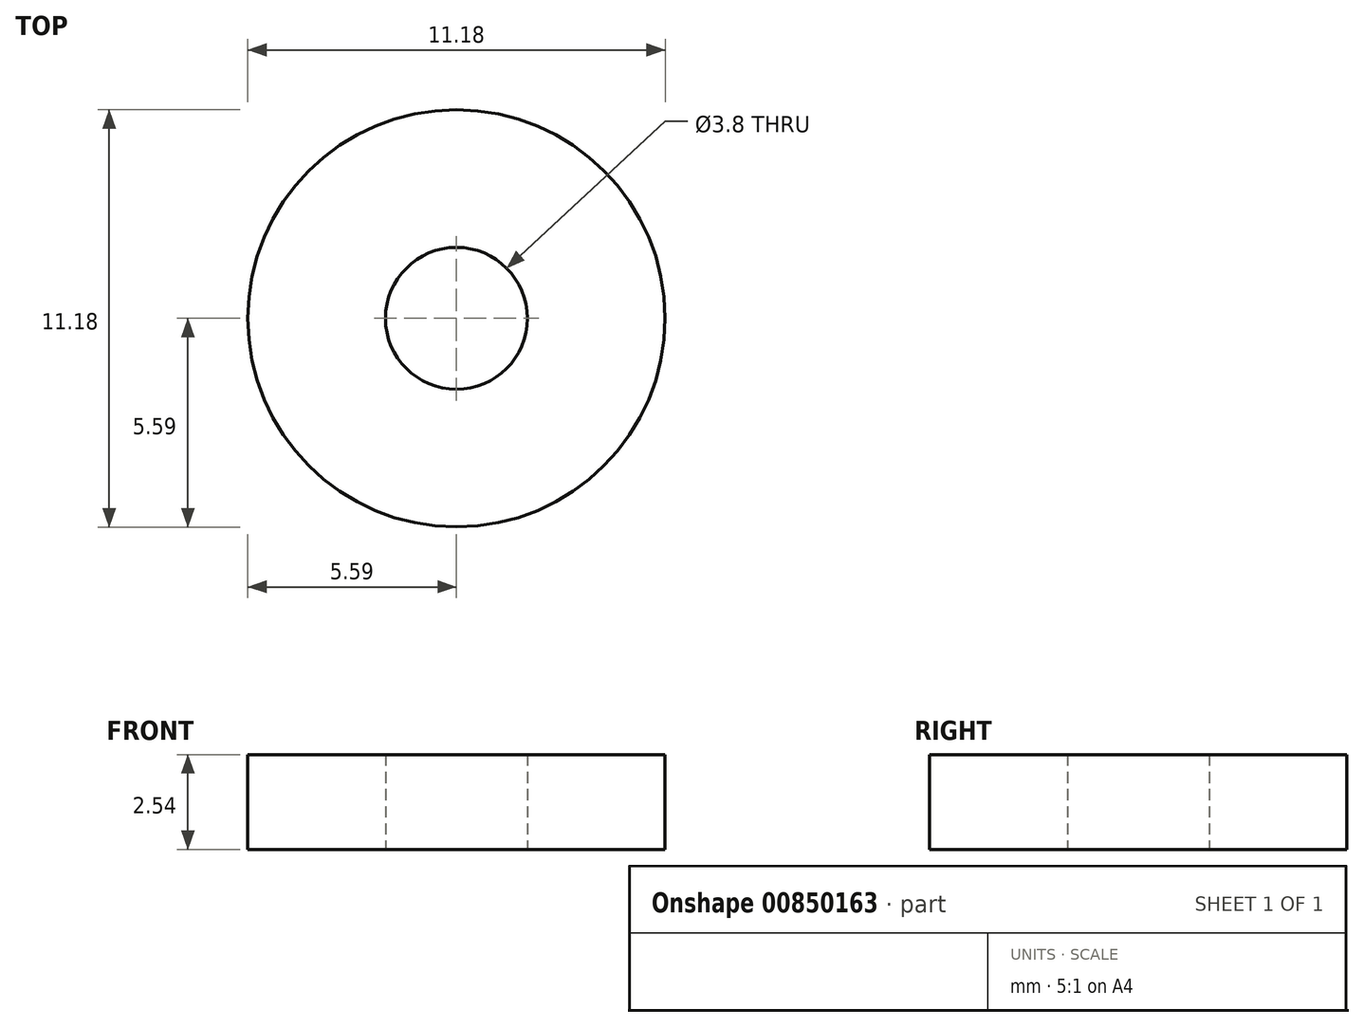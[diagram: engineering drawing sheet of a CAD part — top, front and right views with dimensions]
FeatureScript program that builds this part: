
annotation { "Feature Type Name" : "Feature", "Feature Type Description" : "" }
export const myFeature = defineFeature(function(context is Context, id is Id, definition is map)
    precondition{}
    {
        {
            var Q0;
            Q0=qCreatedBy(makeId("Top.planeOp"),FACE);
            var sketch = newSketch(context, id + "F0", { "sketchPlane" : qUnion([Q0])});
            skCircle(sketch, "E0", {"center": v(0, 0) * mm, "radius": 1.9 * mm});
            skCircle(sketch, "E1", {"center": v(0, 0) * mm, "radius": 5.59 * mm});
            skSolve(sketch);
        }
        {
            var Q0;
            Q0 = qSketchRegion(id + "F0", true);
            extrude(context, id + "F1", {"entities" : qUnion([Q0]), "depth" : 2.54 * mm, "offsetDistance" : 25.4 * mm});
        }
    });
